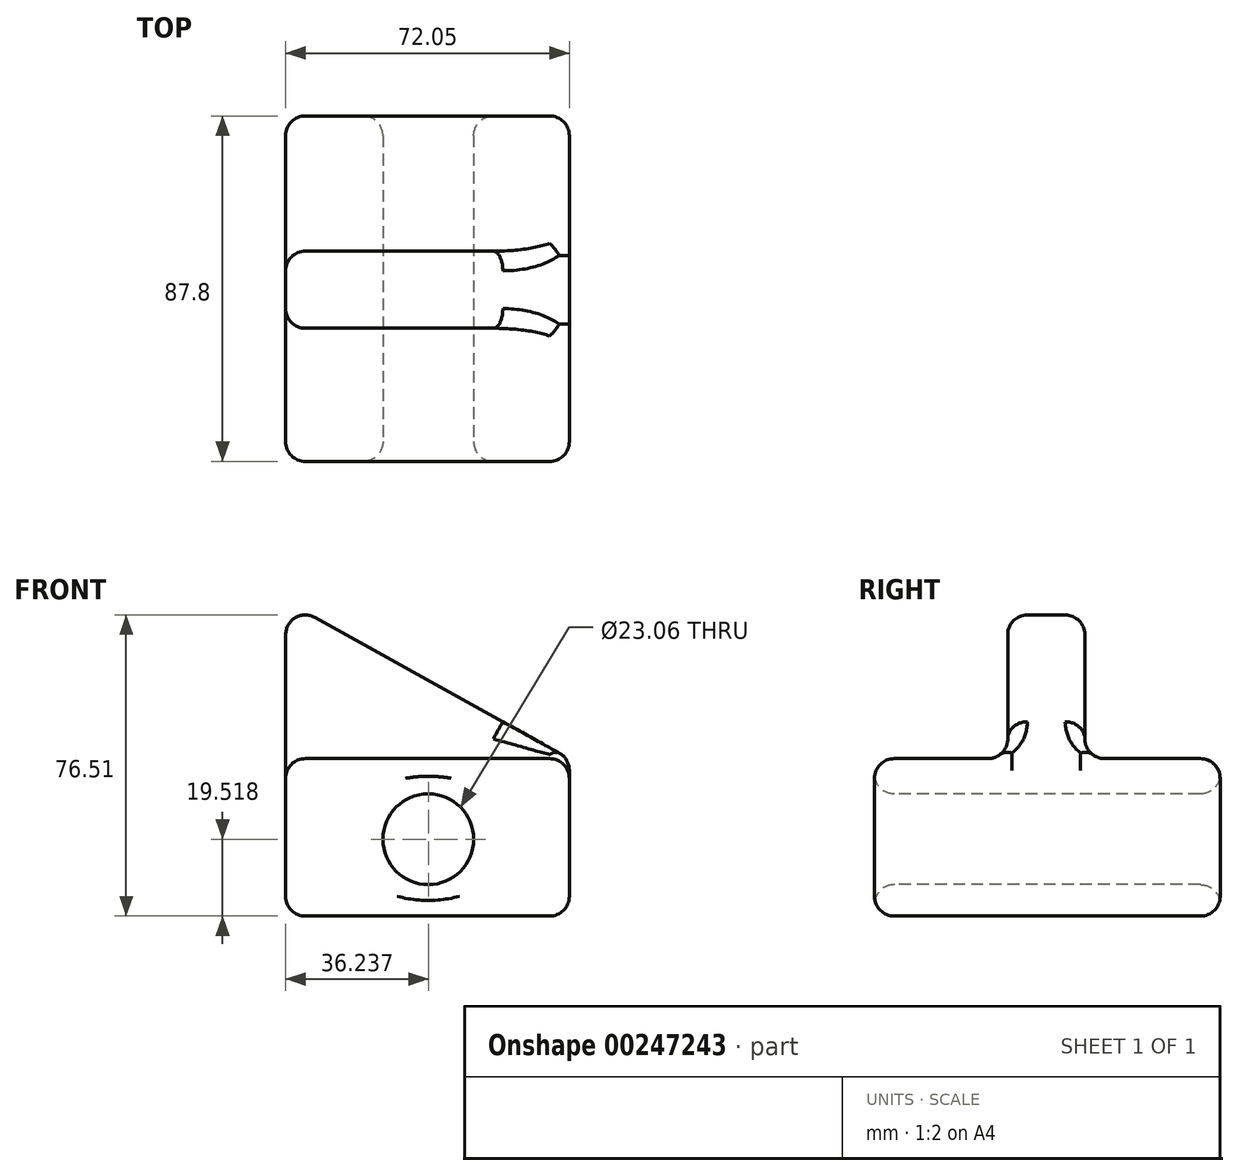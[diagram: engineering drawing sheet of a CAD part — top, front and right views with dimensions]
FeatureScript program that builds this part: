
annotation { "Feature Type Name" : "Feature", "Feature Type Description" : "" }
export const myFeature = defineFeature(function(context is Context, id is Id, definition is map)
    precondition{}
    {
        {
            var Q0;
            Q0=qCreatedBy(makeId("Top.planeOp"),FACE);
            var sketch = newSketch(context, id + "F0", { "sketchPlane" : qUnion([Q0])});
            skLineSegment(sketch, "E0.bottom", {"start": v(-59.89, -44.54) * mm, "end": v(12.16, -44.54) * mm});
            skLineSegment(sketch, "E0.top", {"start": v(-59.89, 43.26) * mm, "end": v(12.16, 43.26) * mm});
            skLineSegment(sketch, "E0.left", {"start": v(-59.89, -44.54) * mm, "end": v(-59.89, 43.26) * mm});
            skLineSegment(sketch, "E0.right", {"start": v(12.16, -44.54) * mm, "end": v(12.16, 43.26) * mm});
            skSolve(sketch);
        }
        {
            var Q0;
            Q0=makeQuery(id+"F0.imprint","IMPRINT",FACE,{"disambiguationData":[TD([[makeQuery(id+"F0.imprint","IMPRINT",EDGE,{"derivedFrom":sQuery(id+"F0.wireOp",EDGE,"E0.bottom")}),1.0]])]});
            extrude(context, id + "F1", {"entities" : qUnion([Q0]), "depth" : 40 * mm});
        }
        {
            var Q0;
            Q0=makeQuery(id+"F1.opExtrude","SWEPT_FACE",FACE,{"disambiguationData":[OSD([sQuery(id+"F0.wireOp",EDGE,"E0.bottom")])]});
            var sketch = newSketch(context, id + "F2", { "sketchPlane" : qUnion([Q0])});
            skCircle(sketch, "E1", {"center": v(-23.65, 19.52) * mm, "radius": 11.53 * mm});
            skSolve(sketch);
        }
        {
            var Q0;
            Q0=makeQuery(id+"F2.imprint","IMPRINT",FACE,{"disambiguationData":[TD([[makeQuery(id+"F2.imprint","IMPRINT",EDGE,{"derivedFrom":sQuery(id+"F2.wireOp",EDGE,"E1")}),1.0]])]});
            extrude(context, id + "F3", {"entities" : qUnion([Q0]), "operationType" : NewBodyOperationType.REMOVE, "endBound" : BoundingType.THROUGH_ALL, "oppositeDirection" : true, "depth" : 25 * mm});
        }
        {
            var Q0;
            Q0=makeQuery(id+"F1.opExtrude","CAP_FACE",FACE,{"disambiguationData":[OSD([sQuery(id+"F0.wireOp",EDGE,"E0.bottom"),sQuery(id+"F0.wireOp",EDGE,"E0.top"),sQuery(id+"F0.wireOp",EDGE,"E0.left"),sQuery(id+"F0.wireOp",EDGE,"E0.right")])],"isStart":false});
            var sketch = newSketch(context, id + "F4", { "sketchPlane" : qUnion([Q0])});
            skLineSegment(sketch, "E2.bottom", {"start": v(-59.89, -10.7) * mm, "end": v(12.16, -10.7) * mm});
            skLineSegment(sketch, "E2.top", {"start": v(-59.89, 8.88) * mm, "end": v(12.16, 8.88) * mm});
            skLineSegment(sketch, "E2.left", {"start": v(-59.89, -10.7) * mm, "end": v(-59.89, 8.88) * mm});
            skLineSegment(sketch, "E2.right", {"start": v(12.16, -10.7) * mm, "end": v(12.16, 8.88) * mm});
            skSolve(sketch);
        }
        {
            var Q0;
            Q0=makeQuery(id+"F4.imprint","IMPRINT",FACE,{"disambiguationData":[TD([[makeQuery(id+"F4.imprint","IMPRINT",EDGE,{"derivedFrom":sQuery(id+"F4.wireOp",EDGE,"E2.bottom")}),1.0]])]});
            extrude(context, id + "F5", {"entities" : qUnion([Q0]), "operationType" : NewBodyOperationType.ADD, "depth" : 40 * mm});
        }
        {
            var Q0;
            Q0=makeQuery(id+"F5.opExtrude","SWEPT_FACE",FACE,{"disambiguationData":[OSD([sQuery(id+"F4.wireOp",EDGE,"E2.bottom")])]});
            var sketch = newSketch(context, id + "F6", { "sketchPlane" : qUnion([Q0])});
            skLineSegment(sketch, "E3", {"start": v(12.16, 40) * mm, "end": v(-59.89, 80) * mm});
            skSolve(sketch);
        }
        {
            var Q0;
            Q0=makeQuery(id+"F6.imprint","IMPRINT",FACE,{"disambiguationData":[TD([[makeQuery(id+"F6.imprint","IMPRINT",EDGE,{"derivedFrom":sQuery(id+"F6.wireOp",EDGE,"E3")}),-1.0]])]});
            extrude(context, id + "F7", {"entities" : qUnion([Q0]), "operationType" : NewBodyOperationType.REMOVE, "endBound" : BoundingType.THROUGH_ALL, "oppositeDirection" : true, "depth" : 25 * mm});
        }
        {
            var Q0;
            Q0=makeQuery(id+"F1.opExtrude","CAP_EDGE",EDGE,{"disambiguationData":[OSD([sQuery(id+"F0.wireOp",EDGE,"E0.top")])],"isStart":false});
            var Q1;
            {var subQ0=sQuery(id+"F0.wireOp",EDGE,"E0.right");var subQ1=sQuery(id+"F0.wireOp",EDGE,"E0.bottom");Q1=makeQuery(id+"F5.boolean.opBoolean","SPLIT",EDGE,{"disambiguationData":[TD([makeQuery(id+"F1.opExtrude","SWEPT_FACE",FACE,{"disambiguationData":[OSD([subQ1])]})])],"derivedFrom":makeQuery(id+"F1.opExtrude","CAP_EDGE",EDGE,{"disambiguationData":[OSD([subQ0])],"isStart":false})});}
            var Q2;
            {var subQ0=sQuery(id+"F0.wireOp",EDGE,"E0.right");var subQ1=sQuery(id+"F0.wireOp",EDGE,"E0.top");Q2=makeQuery(id+"F5.boolean.opBoolean","SPLIT",EDGE,{"disambiguationData":[TD([makeQuery(id+"F1.opExtrude","SWEPT_FACE",FACE,{"disambiguationData":[OSD([subQ1])]})])],"derivedFrom":makeQuery(id+"F1.opExtrude","CAP_EDGE",EDGE,{"disambiguationData":[OSD([subQ0])],"isStart":false})});}
            var Q3;
            Q3=makeQuery(id+"F1.opExtrude","SWEPT_EDGE",EDGE,{"disambiguationData":[OSD([sQuery(id+"F0.wireOp",EDGE,"E0.bottom"),sQuery(id+"F0.wireOp",EDGE,"E0.right")])]});
            var Q4;
            {var subQ0=sQuery(id+"F0.wireOp",EDGE,"E0.left");var subQ1=sQuery(id+"F0.wireOp",EDGE,"E0.bottom");Q4=makeQuery(id+"F5.boolean.opBoolean","SPLIT",EDGE,{"disambiguationData":[TD([makeQuery(id+"F1.opExtrude","SWEPT_FACE",FACE,{"disambiguationData":[OSD([subQ1])]})])],"derivedFrom":makeQuery(id+"F1.opExtrude","CAP_EDGE",EDGE,{"disambiguationData":[OSD([subQ0])],"isStart":false})});}
            var Q5;
            Q5=makeQuery(id+"F5.boolean.opBoolean","MERGE",FACE,{"derivedFrom":[makeQuery(id+"F1.opExtrude","SWEPT_FACE",FACE,{"disambiguationData":[OSD([sQuery(id+"F0.wireOp",EDGE,"E0.left")])]}),makeQuery(id+"F5.opExtrude","SWEPT_FACE",FACE,{"disambiguationData":[OSD([sQuery(id+"F4.wireOp",EDGE,"E2.left")])]})]});
            var Q6;
            Q6=makeQuery(id+"F7.boolean.opBoolean","COPY",FACE,{"derivedFrom":makeQuery(id+"F7.opExtrude","SWEPT_FACE",FACE,{"disambiguationData":[OSD([sQuery(id+"F6.wireOp",EDGE,"E3")])]})});
            var Q7;
            {var subQ0=sQuery(id+"F0.wireOp",EDGE,"E0.right");var subQ1=sQuery(id+"F0.wireOp",EDGE,"E0.left");var subQ2=sQuery(id+"F0.wireOp",EDGE,"E0.top");Q7=makeQuery(id+"F5.boolean.opBoolean","SPLIT",FACE,{"disambiguationData":[TD([makeQuery(id+"F1.opExtrude","SWEPT_FACE",FACE,{"disambiguationData":[OSD([subQ2])]})])],"derivedFrom":makeQuery(id+"F1.opExtrude","CAP_FACE",FACE,{"disambiguationData":[OSD([sQuery(id+"F0.wireOp",EDGE,"E0.bottom"),subQ2,subQ1,subQ0])],"isStart":false})});}
            var Q8;
            Q8=makeQuery(id+"F1.opExtrude","CAP_EDGE",EDGE,{"disambiguationData":[OSD([sQuery(id+"F0.wireOp",EDGE,"E0.bottom")])],"isStart":false});
            var Q9;
            Q9=makeQuery(id+"F7.boolean.opBoolean","INTERSECT",EDGE,{"derivedFrom":[makeQuery(id+"F5.opExtrude","SWEPT_FACE",FACE,{"disambiguationData":[OSD([sQuery(id+"F4.wireOp",EDGE,"E2.top")])]}),makeQuery(id+"F7.opExtrude","SWEPT_FACE",FACE,{"disambiguationData":[OSD([sQuery(id+"F6.wireOp",EDGE,"E3")])]})]});
            var Q10;
            Q10=makeQuery(id+"F3.boolean.opBoolean","COPY",FACE,{"derivedFrom":makeQuery(id+"F3.opExtrude","SWEPT_FACE",FACE,{"disambiguationData":[OSD([sQuery(id+"F2.wireOp",EDGE,"E1")])]})});
            var Q11;
            {var subQ0=sQuery(id+"F4.wireOp",EDGE,"E2.left");Q11=makeQuery(id+"F7.boolean.opBoolean","MERGE",EDGE,{"derivedFrom":[makeQuery(id+"F5.opExtrude","CAP_EDGE",EDGE,{"disambiguationData":[OSD([subQ0])],"isStart":false}),makeQuery(id+"F7.opExtrude","SWEPT_EDGE",EDGE,{"disambiguationData":[OSD([sQuery(id+"F0.wireOp",EDGE,"E0.left"),sQuery(id+"F4.wireOp",EDGE,"E2.bottom"),subQ0,sQuery(id+"F6.wireOp",EDGE,"E3")])]})]});}
            var Q12;
            Q12=makeQuery(id+"F7.boolean.opBoolean","COPY",EDGE,{"derivedFrom":makeQuery(id+"F7.opExtrude","SWEPT_EDGE",EDGE,{"disambiguationData":[OSD([sQuery(id+"F0.wireOp",EDGE,"E0.right"),sQuery(id+"F4.wireOp",EDGE,"E2.bottom"),sQuery(id+"F4.wireOp",EDGE,"E2.right"),sQuery(id+"F6.wireOp",EDGE,"E3")])]})});
            var Q13;
            Q13=makeQuery(id+"F5.opExtrude","SWEPT_FACE",FACE,{"disambiguationData":[OSD([sQuery(id+"F4.wireOp",EDGE,"E2.top")])]});
            var Q14;
            Q14=makeQuery(id+"F1.opExtrude","SWEPT_FACE",FACE,{"disambiguationData":[OSD([sQuery(id+"F0.wireOp",EDGE,"E0.bottom")])]});
            var Q15;
            Q15=makeQuery(id+"F5.boolean.opBoolean","MERGE",FACE,{"derivedFrom":[makeQuery(id+"F1.opExtrude","SWEPT_FACE",FACE,{"disambiguationData":[OSD([sQuery(id+"F0.wireOp",EDGE,"E0.right")])]}),makeQuery(id+"F5.opExtrude","SWEPT_FACE",FACE,{"disambiguationData":[OSD([sQuery(id+"F4.wireOp",EDGE,"E2.right")])]})]});
            var Q16;
            Q16=makeQuery(id+"F5.opExtrude","SWEPT_FACE",FACE,{"disambiguationData":[OSD([sQuery(id+"F4.wireOp",EDGE,"E2.bottom")])]});
            var Q17;
            {var subQ0=sQuery(id+"F0.wireOp",EDGE,"E0.right");var subQ1=sQuery(id+"F0.wireOp",EDGE,"E0.left");var subQ2=sQuery(id+"F0.wireOp",EDGE,"E0.bottom");Q17=makeQuery(id+"F5.boolean.opBoolean","SPLIT",FACE,{"disambiguationData":[TD([makeQuery(id+"F1.opExtrude","SWEPT_FACE",FACE,{"disambiguationData":[OSD([subQ2])]})])],"derivedFrom":makeQuery(id+"F1.opExtrude","CAP_FACE",FACE,{"disambiguationData":[OSD([subQ2,sQuery(id+"F0.wireOp",EDGE,"E0.top"),subQ1,subQ0])],"isStart":false})});}
            var Q18;
            Q18=makeQuery(id+"F1.opExtrude","CAP_FACE",FACE,{"disambiguationData":[OSD([sQuery(id+"F0.wireOp",EDGE,"E0.bottom"),sQuery(id+"F0.wireOp",EDGE,"E0.top"),sQuery(id+"F0.wireOp",EDGE,"E0.left"),sQuery(id+"F0.wireOp",EDGE,"E0.right")])],"isStart":true});
            var Q19;
            Q19=makeQuery(id+"F1.opExtrude","CAP_EDGE",EDGE,{"disambiguationData":[OSD([sQuery(id+"F0.wireOp",EDGE,"E0.right")])],"isStart":true});
            var Q20;
            Q20=makeQuery(id+"F1.opExtrude","CAP_EDGE",EDGE,{"disambiguationData":[OSD([sQuery(id+"F0.wireOp",EDGE,"E0.bottom")])],"isStart":true});
            var Q21;
            Q21=makeQuery(id+"F5.opExtrude","CAP_EDGE",EDGE,{"disambiguationData":[OSD([sQuery(id+"F4.wireOp",EDGE,"E2.bottom")])],"isStart":true});
            var Q22;
            Q22=makeQuery(id+"F7.boolean.opBoolean","COPY",EDGE,{"derivedFrom":makeQuery(id+"F7.opExtrude","CAP_EDGE",EDGE,{"disambiguationData":[OSD([sQuery(id+"F6.wireOp",EDGE,"E3")])],"isStart":true})});
            var Q23;
            Q23=makeQuery(id+"F3.boolean.opBoolean","COPY",EDGE,{"derivedFrom":makeQuery(id+"F3.opExtrude","CAP_EDGE",EDGE,{"disambiguationData":[OSD([sQuery(id+"F2.wireOp",EDGE,"E1")])],"isStart":true})});
            var Q24;
            {var subQ0=sQuery(id+"F0.wireOp",EDGE,"E0.left");var subQ1=sQuery(id+"F0.wireOp",EDGE,"E0.top");Q24=makeQuery(id+"F5.boolean.opBoolean","SPLIT",EDGE,{"disambiguationData":[TD([makeQuery(id+"F1.opExtrude","SWEPT_FACE",FACE,{"disambiguationData":[OSD([subQ1])]})])],"derivedFrom":makeQuery(id+"F1.opExtrude","CAP_EDGE",EDGE,{"disambiguationData":[OSD([subQ0])],"isStart":false})});}
            var Q25;
            Q25=makeQuery(id+"F1.opExtrude","SWEPT_EDGE",EDGE,{"disambiguationData":[OSD([sQuery(id+"F0.wireOp",EDGE,"E0.top"),sQuery(id+"F0.wireOp",EDGE,"E0.left")])]});
            var Q26;
            Q26=makeQuery(id+"F1.opExtrude","CAP_EDGE",EDGE,{"disambiguationData":[OSD([sQuery(id+"F0.wireOp",EDGE,"E0.top")])],"isStart":true});
            var Q27;
            Q27=makeQuery(id+"F1.opExtrude","SWEPT_FACE",FACE,{"disambiguationData":[OSD([sQuery(id+"F0.wireOp",EDGE,"E0.top")])]});
            var Q28;
            Q28=makeQuery(id+"F5.opExtrude","SWEPT_EDGE",EDGE,{"disambiguationData":[OSD([sQuery(id+"F0.wireOp",EDGE,"E0.left"),sQuery(id+"F4.wireOp",EDGE,"E2.top"),sQuery(id+"F4.wireOp",EDGE,"E2.left")])]});
            var Q29;
            Q29=makeQuery(id+"F1.opExtrude","SWEPT_EDGE",EDGE,{"disambiguationData":[OSD([sQuery(id+"F0.wireOp",EDGE,"E0.bottom"),sQuery(id+"F0.wireOp",EDGE,"E0.left")])]});
            var Q30;
            Q30=makeQuery(id+"F5.opExtrude","CAP_EDGE",EDGE,{"disambiguationData":[OSD([sQuery(id+"F4.wireOp",EDGE,"E2.top")])],"isStart":true});
            var Q31;
            Q31=makeQuery(id+"F3.boolean.opBoolean","INTERSECT",EDGE,{"derivedFrom":[makeQuery(id+"F1.opExtrude","SWEPT_FACE",FACE,{"disambiguationData":[OSD([sQuery(id+"F0.wireOp",EDGE,"E0.top")])]}),makeQuery(id+"F3.opExtrude","SWEPT_FACE",FACE,{"disambiguationData":[OSD([sQuery(id+"F2.wireOp",EDGE,"E1")])]})]});
            var Q32;
            Q32=makeQuery(id+"F5.opExtrude","SWEPT_EDGE",EDGE,{"disambiguationData":[OSD([sQuery(id+"F0.wireOp",EDGE,"E0.left"),sQuery(id+"F4.wireOp",EDGE,"E2.bottom"),sQuery(id+"F4.wireOp",EDGE,"E2.left")])]});
            var Q33;
            Q33=makeQuery(id+"F1.opExtrude","SWEPT_EDGE",EDGE,{"disambiguationData":[OSD([sQuery(id+"F0.wireOp",EDGE,"E0.top"),sQuery(id+"F0.wireOp",EDGE,"E0.right")])]});
            var Q34;
            Q34=makeQuery(id+"F1.opExtrude","CAP_EDGE",EDGE,{"disambiguationData":[OSD([sQuery(id+"F0.wireOp",EDGE,"E0.left")])],"isStart":true});
            fillet(context, id + "F8", {"entities" : qUnion([Q0, Q1, Q2, Q3, Q4, Q5, Q6, Q7, Q8, Q9, Q10, Q11, Q12, Q13, Q14, Q15, Q16, Q17, Q18, Q19, Q20, Q21, Q22, Q23, Q24, Q25, Q26, Q27, Q28, Q29, Q30, Q31, Q32, Q33, Q34]), "radius" : 5 * mm, "tangentPropagation" : true, "allowEdgeOverflow" : false});
        }
    });
